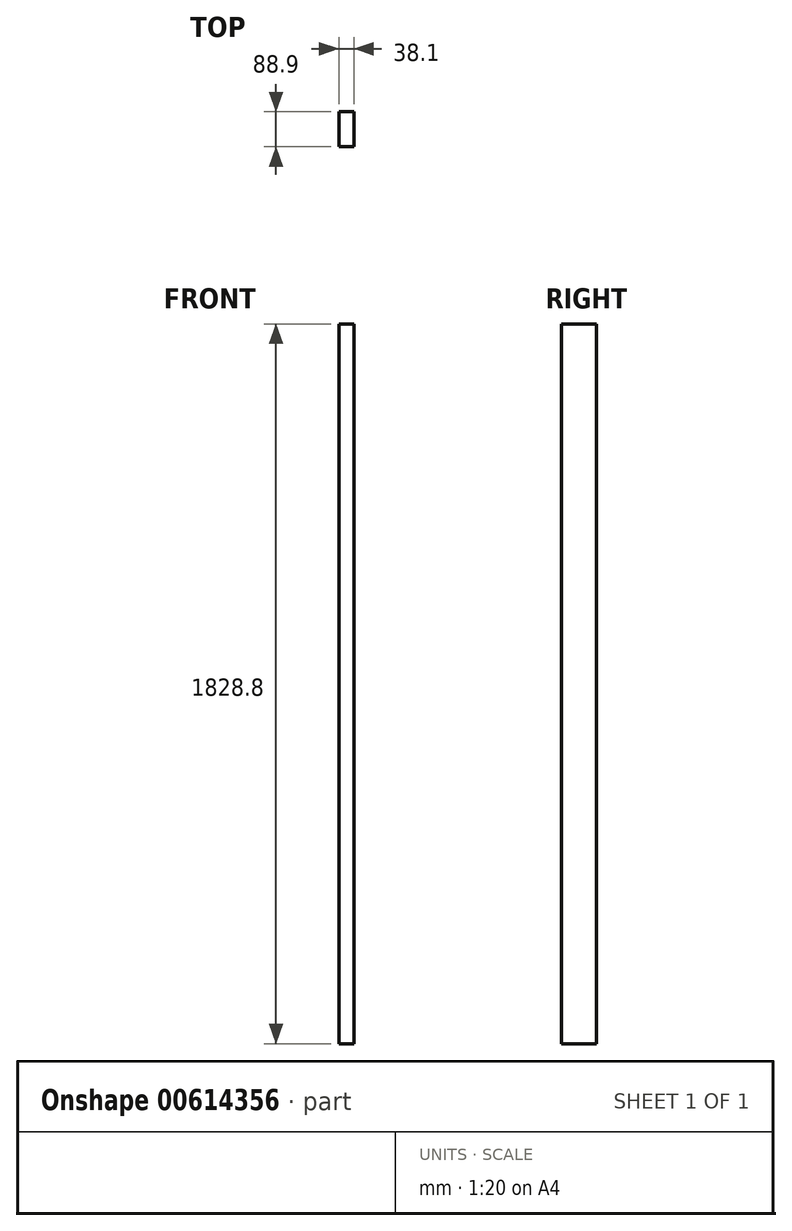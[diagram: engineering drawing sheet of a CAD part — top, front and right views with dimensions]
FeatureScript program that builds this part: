
annotation { "Feature Type Name" : "Feature", "Feature Type Description" : "" }
export const myFeature = defineFeature(function(context is Context, id is Id, definition is map)
    precondition{}
    {
        {
            var Q0;
            Q0=qCreatedBy(makeId("Front.planeOp"),FACE);
            var sketch = newSketch(context, id + "F0", { "sketchPlane" : qUnion([Q0])});
            skLineSegment(sketch, "E0", {"start": v(0, 0) * mm, "end": v(0, 1524) * mm});
            skLineSegment(sketch, "E1", {"start": v(0, 0) * mm, "end": v(0, -304.8) * mm});
            skLineSegment(sketch, "E2", {"start": v(0, -304.8) * mm, "end": v(38.1, -304.8) * mm});
            skLineSegment(sketch, "E3.bottom", {"start": v(38.1, -304.8) * mm, "end": v(0, -304.8) * mm});
            skLineSegment(sketch, "E3.top", {"start": v(38.1, 1524) * mm, "end": v(0, 1524) * mm});
            skLineSegment(sketch, "E3.left", {"start": v(38.1, -304.8) * mm, "end": v(38.1, 1524) * mm});
            skLineSegment(sketch, "E3.right", {"start": v(0, -304.8) * mm, "end": v(0, 1524) * mm});
            skSolve(sketch);
        }
        {
            var Q0;
            Q0=qSketchRegion(id+"F0",true);
            extrude(context, id + "F1", {"entities" : qUnion([Q0]), "depth" : 88.9 * mm, "offsetDistance" : 25.4 * mm});
        }
    });
